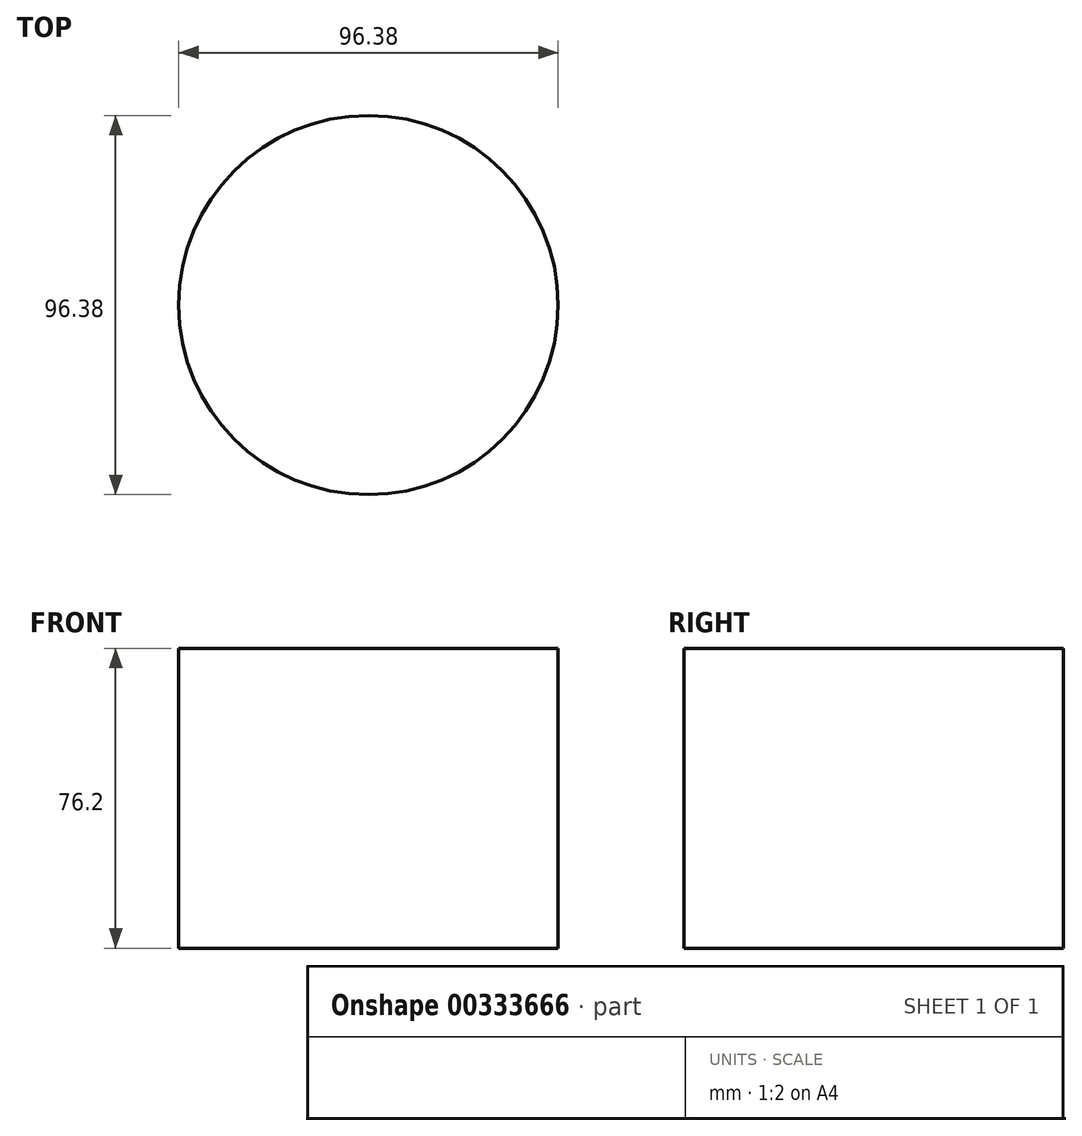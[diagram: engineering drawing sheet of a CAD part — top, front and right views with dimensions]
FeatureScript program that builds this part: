
annotation { "Feature Type Name" : "Feature", "Feature Type Description" : "" }
export const myFeature = defineFeature(function(context is Context, id is Id, definition is map)
    precondition{}
    {
        {
            var Q0;
            Q0=qCreatedBy(makeId("Top.planeOp"),FACE);
            var sketch = newSketch(context, id + "F0", { "sketchPlane" : qUnion([Q0])});
            skCircle(sketch, "E0", {"center": v(0, 0) * mm, "radius": 48.19 * mm});
            skSolve(sketch);
        }
        {
            var Q0;
            Q0 = qSketchRegion(id + "F0", true);
            extrude(context, id + "F1", {"entities" : qUnion([Q0]), "depth" : 76.2 * mm});
        }
    });
